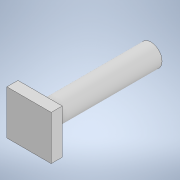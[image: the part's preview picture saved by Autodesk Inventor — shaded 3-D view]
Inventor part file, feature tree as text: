
AUTODESK INVENTOR PART (.ipt)
format: ipt  version: 2022 (Build 260153000, 153)  size: 98,304 bytes
history: native  units: mm
features: extrude x2, sketch x1
ambient origin geometry x8: Origin, YZ Plane, XZ Plane, XY Plane, X Axis, Y Axis, Z Axis, Center Point
bodies: Solid1 (feature_tree)
feature tree (3):
  sketch  "Sketch1"  dims[d0=40.0mm d2=20.0mm d4=10.0mm d5=0.0mm d8=100.0mm d9=0.0mm]
  extrude  "Extrusion1"  Depth=100.0mm
  extrude  "Extrusion3"  Depth=10.0mm TaperAngle=0.0deg
